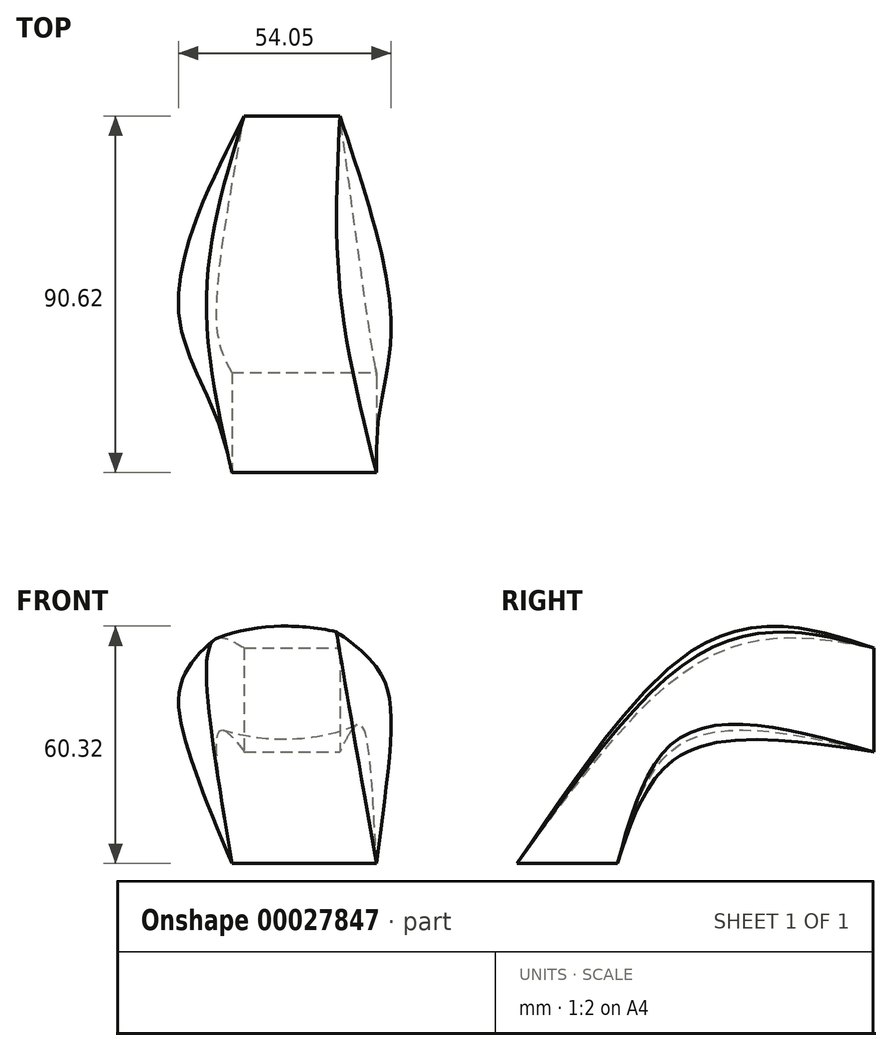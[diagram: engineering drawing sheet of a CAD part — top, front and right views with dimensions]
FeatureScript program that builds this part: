
annotation { "Feature Type Name" : "Feature", "Feature Type Description" : "" }
export const myFeature = defineFeature(function(context is Context, id is Id, definition is map)
    precondition{}
    {
        {
            var Q0;
            Q0=qCreatedBy(makeId("Top.planeOp"),FACE);
            var sketch = newSketch(context, id + "F0", { "sketchPlane" : qUnion([Q0])});
            skLineSegment(sketch, "E0.bottom", {"start": v(-46.43, -15.14) * mm, "end": v(-9.75, -15.14) * mm});
            skLineSegment(sketch, "E0.top", {"start": v(-46.43, -40.62) * mm, "end": v(-9.75, -40.62) * mm});
            skLineSegment(sketch, "E0.left", {"start": v(-46.43, -15.14) * mm, "end": v(-46.43, -40.62) * mm});
            skLineSegment(sketch, "E0.right", {"start": v(-9.75, -15.14) * mm, "end": v(-9.75, -40.62) * mm});
            skSolve(sketch);
        }
        {
            var Q0;
            Q0=qCreatedBy(makeId("Front.planeOp"),FACE);
            var sketch = newSketch(context, id + "F1", { "sketchPlane" : qUnion([Q0])});
            skEllipticalArc(sketch, "E1", {});
            skEllipticalArc(sketch, "E2", {});
            skEllipticalArc(sketch, "E3", {});
            skEllipticalArc(sketch, "E4", {});
            const initialGuessF1  = {"E1": [-0.032995402812957764, 0.03912420570850372, 1, 0, 0.026915574446320534, 0.0121906232999198, 0.9932104283188689, 2.402811746302253], "E2": [-0.032995402812957764, 0.03912420570850372, 1, 0, 0.026915574446320534, 0.0121906232999198, 2.402811746302253, 4.013134098199821], "E3": [-0.032995402812957764, 0.03912420570850372, 1, 0, 0.026915574446320534, 0.0121906232999198, 5.5993222580383435, 0.9932104283188689], "E4": [-0.032995402812957764, 0.03912420570850372, 1, 0, 0.026915574446320534, 0.0121906232999198, 4.013134098199821, 5.5993222580383435]};
            skSetInitialGuess(sketch, initialGuessF1);
            skSolve(sketch);
        }
        {
            var Q0;
            Q0=qCreatedBy(makeId("Right.planeOp"),FACE);
            cPlane(context, id + "F2", {"entities" : qUnion([Q0]), "cplaneType" : CPlaneType.OFFSET, "offset" : 20 * mm, "oppositeDirection" : true, "width" : 150 * mm, "height" : 150 * mm});
        }
        {
            var Q0;
            Q0=qCreatedBy(makeId("Front.planeOp"),FACE);
            cPlane(context, id + "F3", {"entities" : qUnion([Q0]), "cplaneType" : CPlaneType.OFFSET, "offset" : 50 * mm, "oppositeDirection" : true, "width" : 150 * mm, "height" : 150 * mm});
        }
        {
            var Q0;
            Q0=qCreatedBy(id+"F3.planeOp",FACE);
            var sketch = newSketch(context, id + "F4", { "sketchPlane" : qUnion([Q0])});
            skLineSegment(sketch, "E5.bottom", {"start": v(-43.28, 54.77) * mm, "end": v(-18.99, 54.77) * mm});
            skLineSegment(sketch, "E5.top", {"start": v(-43.28, 28.37) * mm, "end": v(-18.99, 28.37) * mm});
            skLineSegment(sketch, "E5.left", {"start": v(-43.28, 54.77) * mm, "end": v(-43.28, 28.37) * mm});
            skLineSegment(sketch, "E5.right", {"start": v(-18.99, 54.77) * mm, "end": v(-18.99, 28.37) * mm});
            skSolve(sketch);
        }
        {
            var Q0;
            Q0=makeQuery(id+"F0.imprint","IMPRINT",FACE,{"disambiguationData":[TD([[makeQuery(id+"F0.imprint","IMPRINT",EDGE,{"derivedFrom":sQuery(id+"F0.wireOp",EDGE,"E0.bottom")}),-1.0]])]});
            var Q1;
            Q1=makeQuery(id+"F1.imprint","IMPRINT",FACE,{"disambiguationData":[TD([[makeQuery(id+"F1.imprint","IMPRINT",EDGE,{"derivedFrom":sQuery(id+"F1.wireOp",EDGE,"E1")}),1.0]])]});
            var Q2;
            Q2=makeQuery(id+"F4.imprint","IMPRINT",FACE,{"disambiguationData":[TD([[makeQuery(id+"F4.imprint","IMPRINT",EDGE,{"derivedFrom":sQuery(id+"F4.wireOp",EDGE,"E5.bottom")}),-1.0]])]});
            loft(context, id + "F5", {"sheetProfilesArray" : [{ "sheetProfileEntities" : qUnion([Q0]) }, { "sheetProfileEntities" : qUnion([Q1]) }, { "sheetProfileEntities" : qUnion([Q2]) }]});
        }
    });
